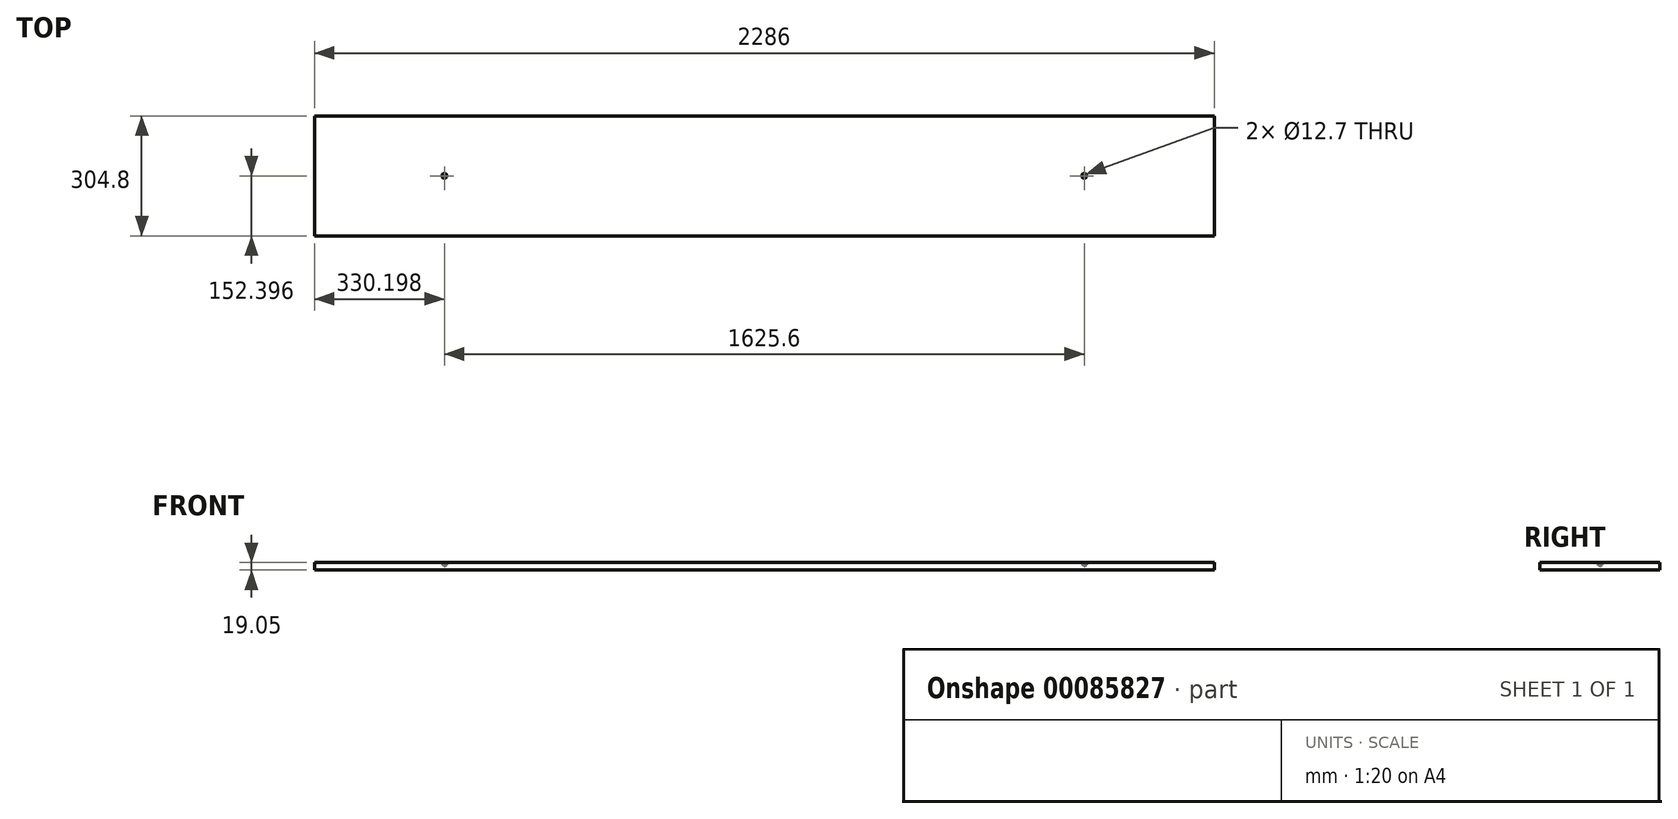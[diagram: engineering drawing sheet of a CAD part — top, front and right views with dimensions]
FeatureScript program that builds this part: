
annotation { "Feature Type Name" : "Feature", "Feature Type Description" : "" }
export const myFeature = defineFeature(function(context is Context, id is Id, definition is map)
    precondition{}
    {
        {
            var Q0;
            Q0=qCreatedBy(makeId("Top.planeOp"),FACE);
            var sketch = newSketch(context, id + "F0", { "sketchPlane" : qUnion([Q0])});
            skLineSegment(sketch, "E0.bottom", {"start": v(-1151.53, 170.53) * mm, "end": v(1134.47, 170.53) * mm});
            skLineSegment(sketch, "E0.top", {"start": v(-1151.53, -134.27) * mm, "end": v(1134.47, -134.27) * mm});
            skLineSegment(sketch, "E0.left", {"start": v(-1151.53, 170.53) * mm, "end": v(-1151.53, -134.27) * mm});
            skLineSegment(sketch, "E0.right", {"start": v(1134.47, 170.53) * mm, "end": v(1134.47, -134.27) * mm});
            skSolve(sketch);
        }
        {
            var Q0;
            Q0=makeQuery(id+"F0.imprint","IMPRINT",FACE,{"disambiguationData":[TD([[makeQuery(id+"F0.imprint","IMPRINT",EDGE,{"derivedFrom":sQuery(id+"F0.wireOp",EDGE,"E0.bottom")}),-1.0]])]});
            extrude(context, id + "F1", {"entities" : qUnion([Q0]), "depth" : 19.05 * mm, "offsetDistance" : 25.4 * mm});
        }
        {
            var Q0;
            Q0=makeQuery(id+"F1.opExtrude","CAP_FACE",FACE,{"disambiguationData":[OSD([sQuery(id+"F0.wireOp",EDGE,"E0.bottom"),sQuery(id+"F0.wireOp",EDGE,"E0.top"),sQuery(id+"F0.wireOp",EDGE,"E0.left"),sQuery(id+"F0.wireOp",EDGE,"E0.right")])],"isStart":false});
            var sketch = newSketch(context, id + "F2", { "sketchPlane" : qUnion([Q0])});
            skPoint(sketch, "E1", {"position": v(-821.33, 18.13) * mm});
            skPoint(sketch, "E1.positionSnap0", {"position": v(-1151.53, 18.13) * mm});
            skPoint(sketch, "E2", {"position": v(804.27, 18.13) * mm});
            skPoint(sketch, "E2.positionSnap0", {"position": v(1134.47, 18.13) * mm});
            skSolve(sketch);
        }
        {
            var Q0;
            Q0=sQuery(id+"F2.wireOp",VERTEX,"E1");
            var Q1;
            Q1=sQuery(id+"F2.wireOp",VERTEX,"E2");
            var Q2;
            Q2=makeQuery(id+"F1.opExtrude","SWEPT_BODY",BODY,{"disambiguationData":[OSD([sQuery(id+"F0.wireOp",EDGE,"E0.bottom"),sQuery(id+"F0.wireOp",EDGE,"E0.top"),sQuery(id+"F0.wireOp",EDGE,"E0.left"),sQuery(id+"F0.wireOp",EDGE,"E0.right")])]});
            hole(context, id + "F3", {"style" : HoleStyle.SIMPLE, "endStyle" : HoleEndStyle.BLIND, "holeDiameter" : 12.7 * mm, "majorDiameter" : 6.35 * mm, "holeDepth" : 6.35 * mm, "isTappedThrough" : true, "tappedDepth" : 19.05 * mm, "tapClearance" : 3, "locations" : qUnion([Q0, Q1]), "scope" : qUnion([Q2])});
        }
    });
